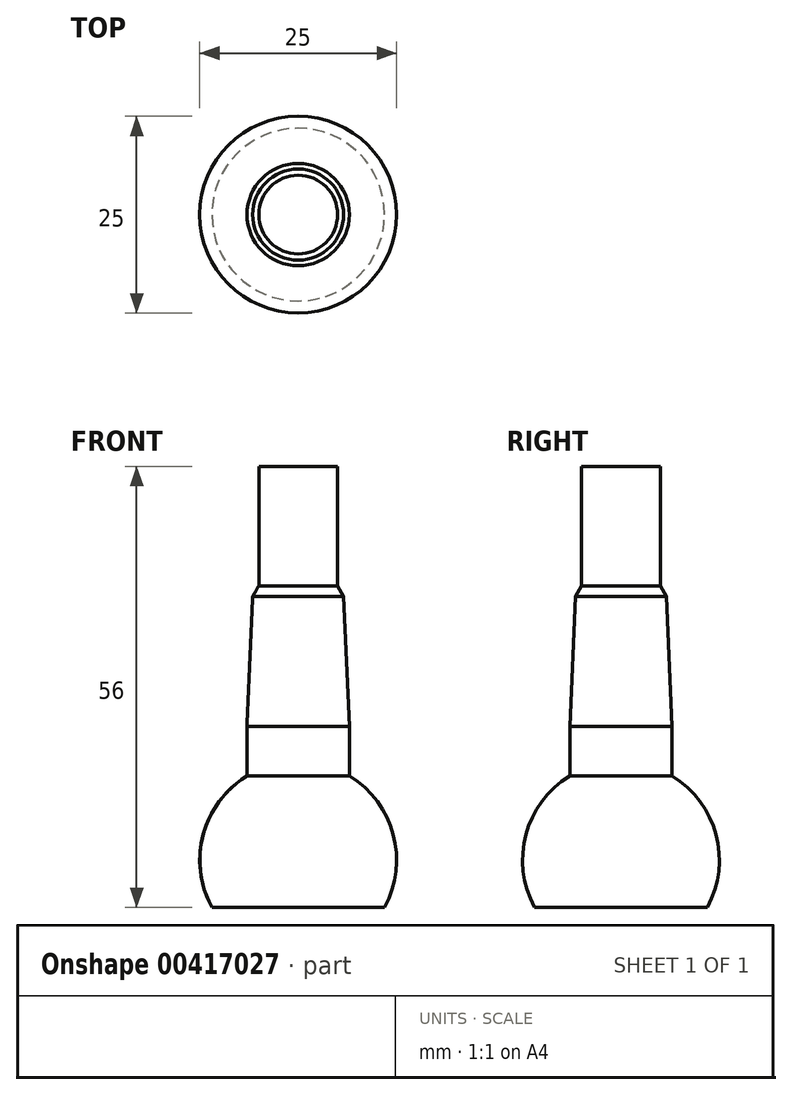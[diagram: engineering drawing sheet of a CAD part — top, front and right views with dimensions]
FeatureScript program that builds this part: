
annotation { "Feature Type Name" : "Feature", "Feature Type Description" : "" }
export const myFeature = defineFeature(function(context is Context, id is Id, definition is map)
    precondition{}
    {
        {
            var Q0;
            Q0=qCreatedBy(makeId("Front.planeOp"),FACE);
            var sketch = newSketch(context, id + "F0", { "sketchPlane" : qUnion([Q0])});
            skArc(sketch, "E0", {"start": v(-6.5, 10.68) * mm, "mid": v(-12.07, 3.23) * mm, "end": v(-10.97, -6) * mm});
            skLineSegment(sketch, "E1", {"start": v(0, -37.1) * mm, "end": v(0, 77.97) * mm, "construction": true});
            skLineSegment(sketch, "E2", {"start": v(-6.5, 10.68) * mm, "end": v(-6.5, 17) * mm});
            skLineSegment(sketch, "E3", {"start": v(-6.5, 17) * mm, "end": v(-5.78, 33.5) * mm});
            skLineSegment(sketch, "E4", {"start": v(-5.78, 33.5) * mm, "end": v(-5, 34.85) * mm});
            skLineSegment(sketch, "E5", {"start": v(-5, 34.85) * mm, "end": v(-5, 50) * mm});
            skLineSegment(sketch, "E6", {"start": v(-5, 50) * mm, "end": v(0, 50) * mm});
            skLineSegment(sketch, "E7", {"start": v(0, 50) * mm, "end": v(0, -12.5) * mm});
            skLineSegment(sketch, "E8", {"start": v(-10.97, -6) * mm, "end": v(0, -6) * mm});
            skSolve(sketch);
        }
        {
            var Q0;
            Q0 = qSketchRegion(id + "F0", true);
            var Q1;
            Q1=sQuery(id+"F0.wireOp",EDGE,"E1");
            revolve(context, id + "F1", {"entities" : qUnion([Q0]), "axis" : qUnion([Q1]), "revolveType" : RevolveType.FULL});
        }
    });
